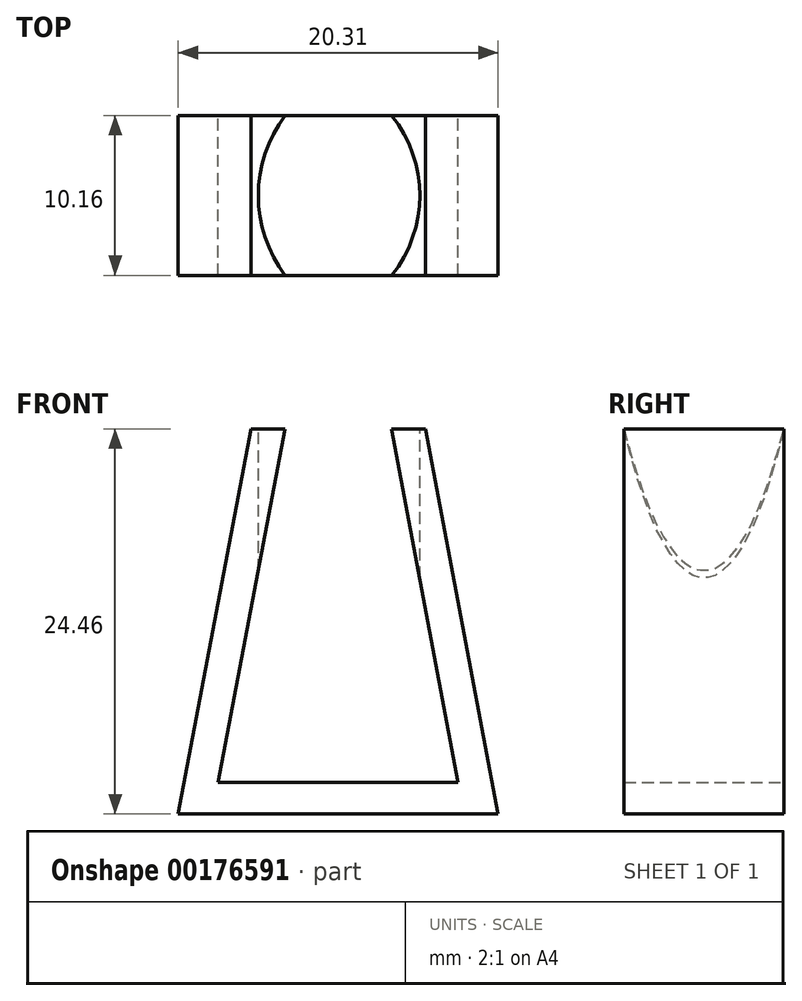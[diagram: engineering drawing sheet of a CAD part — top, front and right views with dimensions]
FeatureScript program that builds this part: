
annotation { "Feature Type Name" : "Feature", "Feature Type Description" : "" }
export const myFeature = defineFeature(function(context is Context, id is Id, definition is map)
    precondition{}
    {
        {
            var Q0;
            Q0=qCreatedBy(makeId("Front.planeOp"),FACE);
            var sketch = newSketch(context, id + "F0", { "sketchPlane" : qUnion([Q0])});
            skLineSegment(sketch, "E0", {"start": v(0, 0) * mm, "end": v(-10.16, 0) * mm});
            skLineSegment(sketch, "E1", {"start": v(-10.16, 0) * mm, "end": v(-5.53, 24.46) * mm});
            skLineSegment(sketch, "E2", {"start": v(-5.53, 24.46) * mm, "end": v(-3.37, 24.46) * mm});
            skLineSegment(sketch, "E3", {"start": v(-3.37, 24.46) * mm, "end": v(-7.62, 2) * mm});
            skLineSegment(sketch, "E4", {"start": v(-7.62, 2) * mm, "end": v(0, 2) * mm});
            skLineSegment(sketch, "E5", {"start": v(0, 0) * mm, "end": v(10.15, 0) * mm});
            skLineSegment(sketch, "E6", {"start": v(10.15, 0) * mm, "end": v(5.56, 24.46) * mm});
            skLineSegment(sketch, "E7", {"start": v(5.56, 24.46) * mm, "end": v(3.4, 24.46) * mm});
            skLineSegment(sketch, "E8", {"start": v(0, 2) * mm, "end": v(7.62, 2) * mm});
            skLineSegment(sketch, "E9", {"start": v(7.62, 2) * mm, "end": v(3.4, 24.46) * mm});
            skSolve(sketch);
        }
        {
            var Q0;
            Q0=makeQuery(id+"F0.imprint","IMPRINT",FACE,{"disambiguationData":[TD([[makeQuery(id+"F0.imprint","IMPRINT",EDGE,{"derivedFrom":sQuery(id+"F0.wireOp",EDGE,"E0")}),-1.0]])]});
            extrude(context, id + "F1", {"entities" : qUnion([Q0]), "depth" : 10.16 * mm});
        }
        {
            var Q0;
            Q0=makeQuery(id+"F1.opExtrude","SWEPT_FACE",FACE,{"disambiguationData":[OSD([sQuery(id+"F0.wireOp",EDGE,"E2")])]});
            var sketch = newSketch(context, id + "F2", { "sketchPlane" : qUnion([Q0])});
            skArc(sketch, "E10", {"start": v(-3.37, 0) * mm, "mid": v(-5.07, -5.08) * mm, "end": v(-3.37, -10.16) * mm});
            skLineSegment(sketch, "E11", {"start": v(-3.37, 0) * mm, "end": v(-3.37, -10.16) * mm});
            skSolve(sketch);
        }
        {
            var Q0;
            Q0=makeQuery(id+"F2.imprint","IMPRINT",FACE,{"disambiguationData":[TD([[makeQuery(id+"F2.imprint","IMPRINT",EDGE,{"derivedFrom":sQuery(id+"F2.wireOp",EDGE,"E10")}),1.0]])]});
            extrude(context, id + "F3", {"entities" : qUnion([Q0]), "operationType" : NewBodyOperationType.REMOVE, "oppositeDirection" : true, "depth" : 20.32 * mm});
        }
        {
            var Q0;
            Q0=makeQuery(id+"F1.opExtrude","SWEPT_FACE",FACE,{"disambiguationData":[OSD([sQuery(id+"F0.wireOp",EDGE,"E7")])]});
            var sketch = newSketch(context, id + "F4", { "sketchPlane" : qUnion([Q0])});
            skArc(sketch, "E12", {"start": v(3.4, -10.16) * mm, "mid": v(5.18, -5.08) * mm, "end": v(3.4, 0) * mm});
            skLineSegment(sketch, "E13", {"start": v(3.4, 0) * mm, "end": v(3.4, -10.16) * mm});
            skSolve(sketch);
        }
        {
            var Q0;
            Q0=makeQuery(id+"F4.imprint","IMPRINT",FACE,{"disambiguationData":[TD([[makeQuery(id+"F4.imprint","IMPRINT",EDGE,{"derivedFrom":sQuery(id+"F4.wireOp",EDGE,"E12")}),1.0]])]});
            extrude(context, id + "F5", {"entities" : qUnion([Q0]), "operationType" : NewBodyOperationType.REMOVE, "oppositeDirection" : true, "depth" : 20.32 * mm});
        }
    });
